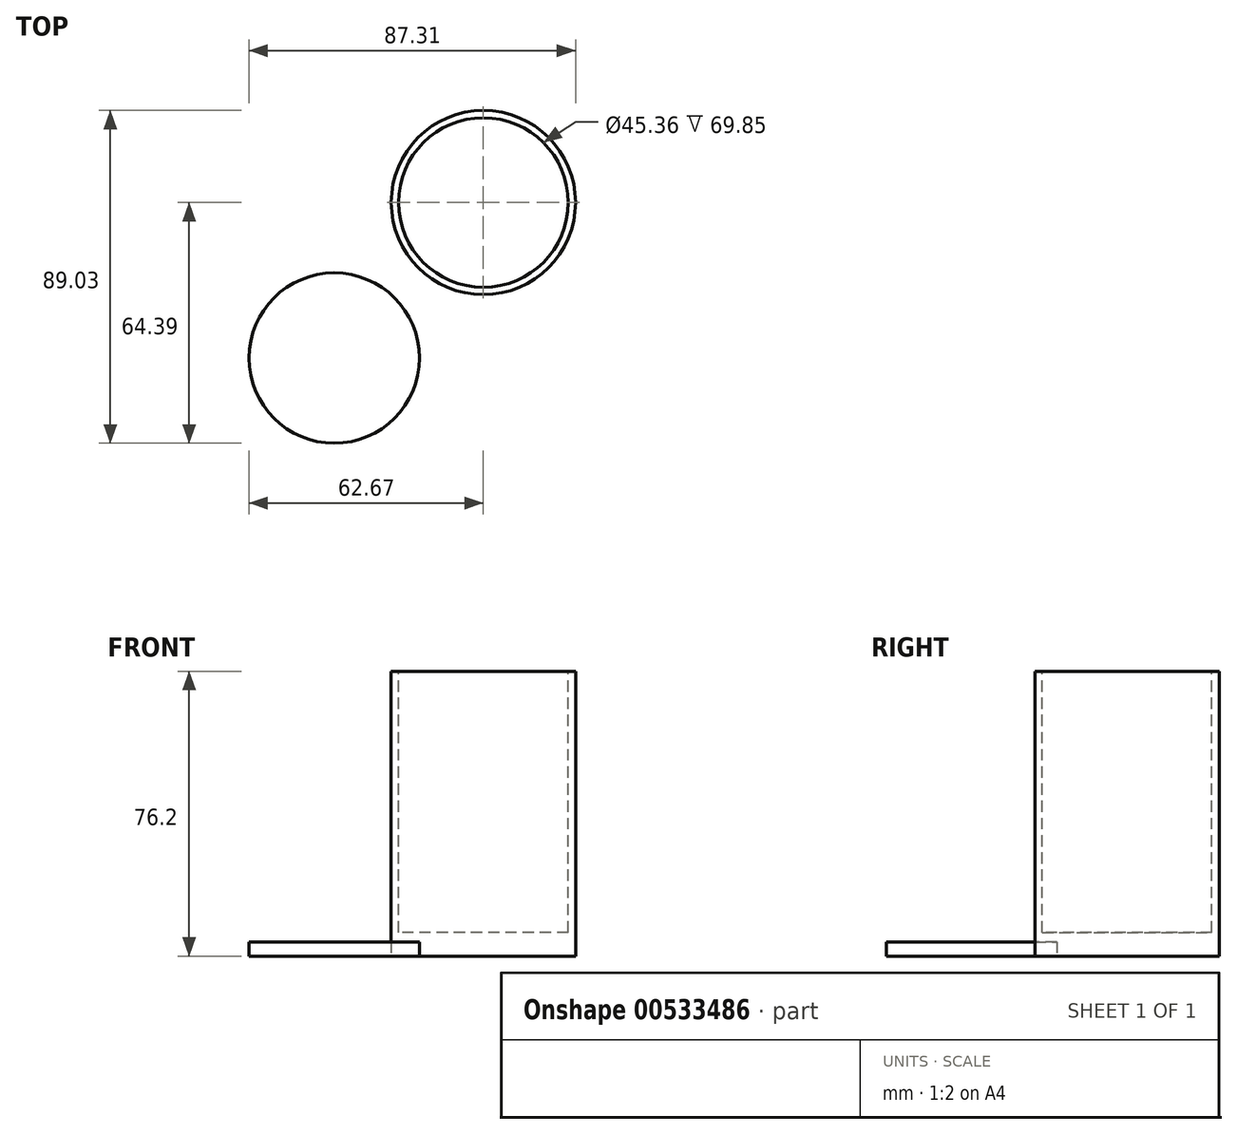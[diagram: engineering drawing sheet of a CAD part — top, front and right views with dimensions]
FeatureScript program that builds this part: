
annotation { "Feature Type Name" : "Feature", "Feature Type Description" : "" }
export const myFeature = defineFeature(function(context is Context, id is Id, definition is map)
    precondition{}
    {
        {
            var Q0;
            Q0=qCreatedBy(makeId("Top.planeOp"),FACE);
            var sketch = newSketch(context, id + "F0", { "sketchPlane" : qUnion([Q0])});
            skCircle(sketch, "E0", {"center": v(0, 0) * mm, "radius": 24.64 * mm});
            skSolve(sketch);
        }
        {
            var Q0;
            Q0=makeQuery(id+"F0.imprint","IMPRINT",FACE,{"disambiguationData":[TD([[makeQuery(id+"F0.imprint","IMPRINT",EDGE,{"derivedFrom":sQuery(id+"F0.wireOp",EDGE,"E0")}),1.0]])]});
            extrude(context, id + "F1", {"entities" : qUnion([Q0]), "depth" : 76.2 * mm, "offsetDistance" : 25.4 * mm});
        }
        {
            var Q0;
            Q0=makeQuery(id+"F1.opExtrude","CAP_FACE",FACE,{"disambiguationData":[OSD([sQuery(id+"F0.wireOp",EDGE,"E0")])],"isStart":false});
            var sketch = newSketch(context, id + "F2", { "sketchPlane" : qUnion([Q0])});
            skCircle(sketch, "E1", {"center": v(0, 0) * mm, "radius": 22.68 * mm});
            skSolve(sketch);
        }
        {
            var Q0;
            Q0=makeQuery(id+"F2.imprint","IMPRINT",FACE,{"disambiguationData":[TD([[makeQuery(id+"F2.imprint","IMPRINT",EDGE,{"derivedFrom":sQuery(id+"F2.wireOp",EDGE,"E1")}),1.0]])]});
            extrude(context, id + "F3", {"entities" : qUnion([Q0]), "operationType" : NewBodyOperationType.REMOVE, "oppositeDirection" : true, "depth" : 69.85 * mm, "offsetDistance" : 25.4 * mm});
        }
        {
            var Q0;
            Q0=qCreatedBy(makeId("Top.planeOp"),FACE);
            var sketch = newSketch(context, id + "F4", { "sketchPlane" : qUnion([Q0])});
            skCircle(sketch, "E2", {"center": v(-39.89, -41.6) * mm, "radius": 22.79 * mm});
            skSolve(sketch);
        }
        {
            var Q0;
            Q0=makeQuery(id+"F4.imprint","IMPRINT",FACE,{"disambiguationData":[TD([[makeQuery(id+"F4.imprint","IMPRINT",EDGE,{"derivedFrom":sQuery(id+"F4.wireOp",EDGE,"E2")}),1.0]])]});
            extrude(context, id + "F5", {"entities" : qUnion([Q0]), "depth" : 3.8 * mm, "offsetDistance" : 25.4 * mm});
        }
    });
